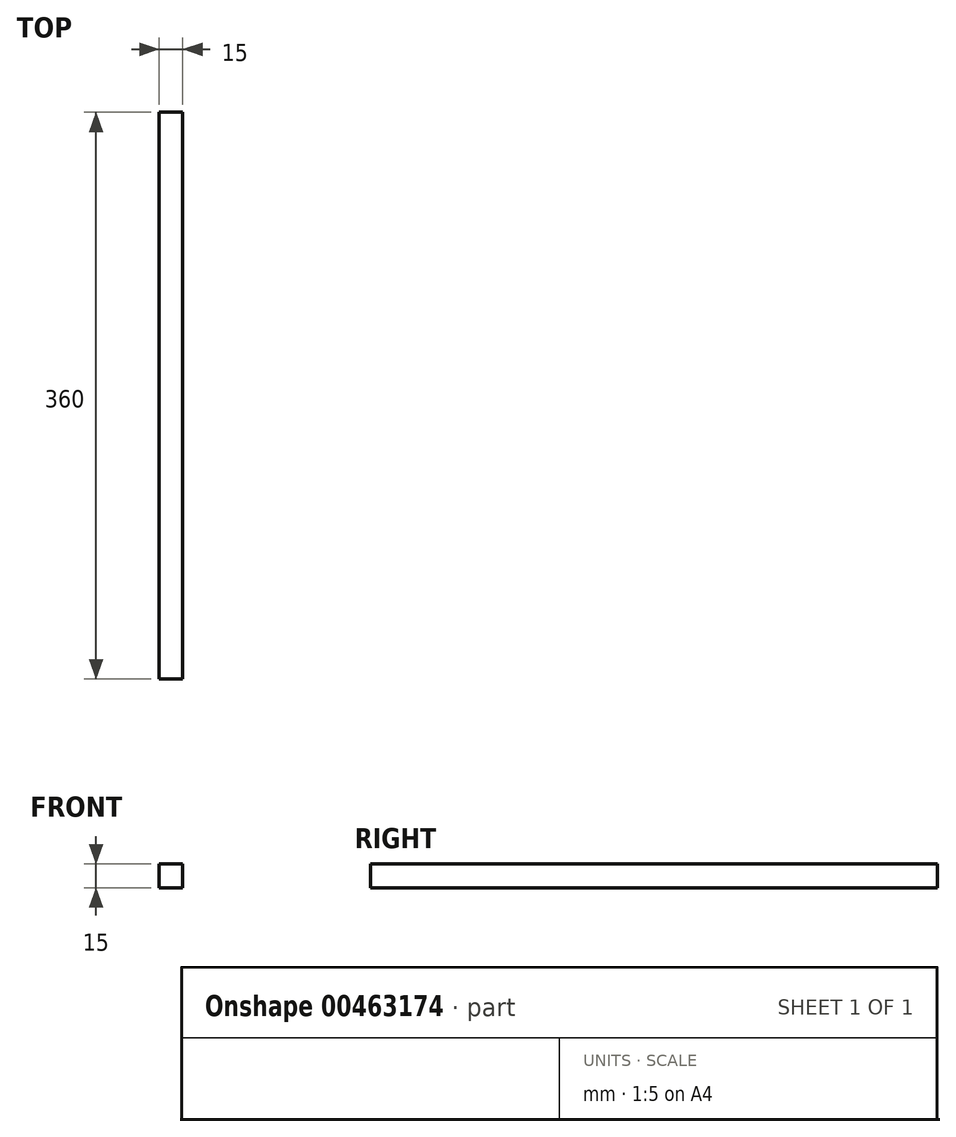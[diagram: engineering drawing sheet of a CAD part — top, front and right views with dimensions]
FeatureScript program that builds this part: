
annotation { "Feature Type Name" : "Feature", "Feature Type Description" : "" }
export const myFeature = defineFeature(function(context is Context, id is Id, definition is map)
    precondition{}
    {
        {
            var Q0;
            Q0=qCreatedBy(makeId("Front.planeOp"),FACE);
            var sketch = newSketch(context, id + "F0", { "sketchPlane" : qUnion([Q0])});
            skLineSegment(sketch, "E0.bottom", {"start": v(0, 0) * mm, "end": v(15, 0) * mm});
            skLineSegment(sketch, "E0.top", {"start": v(0, 15) * mm, "end": v(15, 15) * mm});
            skLineSegment(sketch, "E0.left", {"start": v(0, 0) * mm, "end": v(0, 15) * mm});
            skLineSegment(sketch, "E0.right", {"start": v(15, 0) * mm, "end": v(15, 15) * mm});
            skSolve(sketch);
        }
        {
            var Q0;
            Q0 = qSketchRegion(id + "F0", true);
            extrude(context, id + "F1", {"entities" : qUnion([Q0]), "depth" : 360 * mm});
        }
    });
